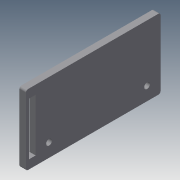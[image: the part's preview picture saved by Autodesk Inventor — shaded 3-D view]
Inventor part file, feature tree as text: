
AUTODESK INVENTOR PART (.ipt)
format: ipt  version: 2014 (Build 180170000, 170)  size: 93,184 bytes
history: native  units: mm
features: extrude x1, fillet x1, sketch x1
ambient origin geometry x8: Origin, YZ Plane, XZ Plane, XY Plane, X Axis, Y Axis, Z Axis, Center Point
bodies: Solid1 (feature_tree)
feature tree (3):
  extrude  "Extrusion1"  Depth=125.0mm
  fillet  "Fillet1"  Radius=6.25mm
  sketch  "Sketch1"  dims[d0=65.0mm d1=125.0mm d2=6.25mm d3=2.875mm d4=8.1mm d5=8.1mm d6=12.5mm d7=21.5mm d8=12.5mm d9=5.4mm d10=6.0mm d11=0.0mm d12=2.0mm]
